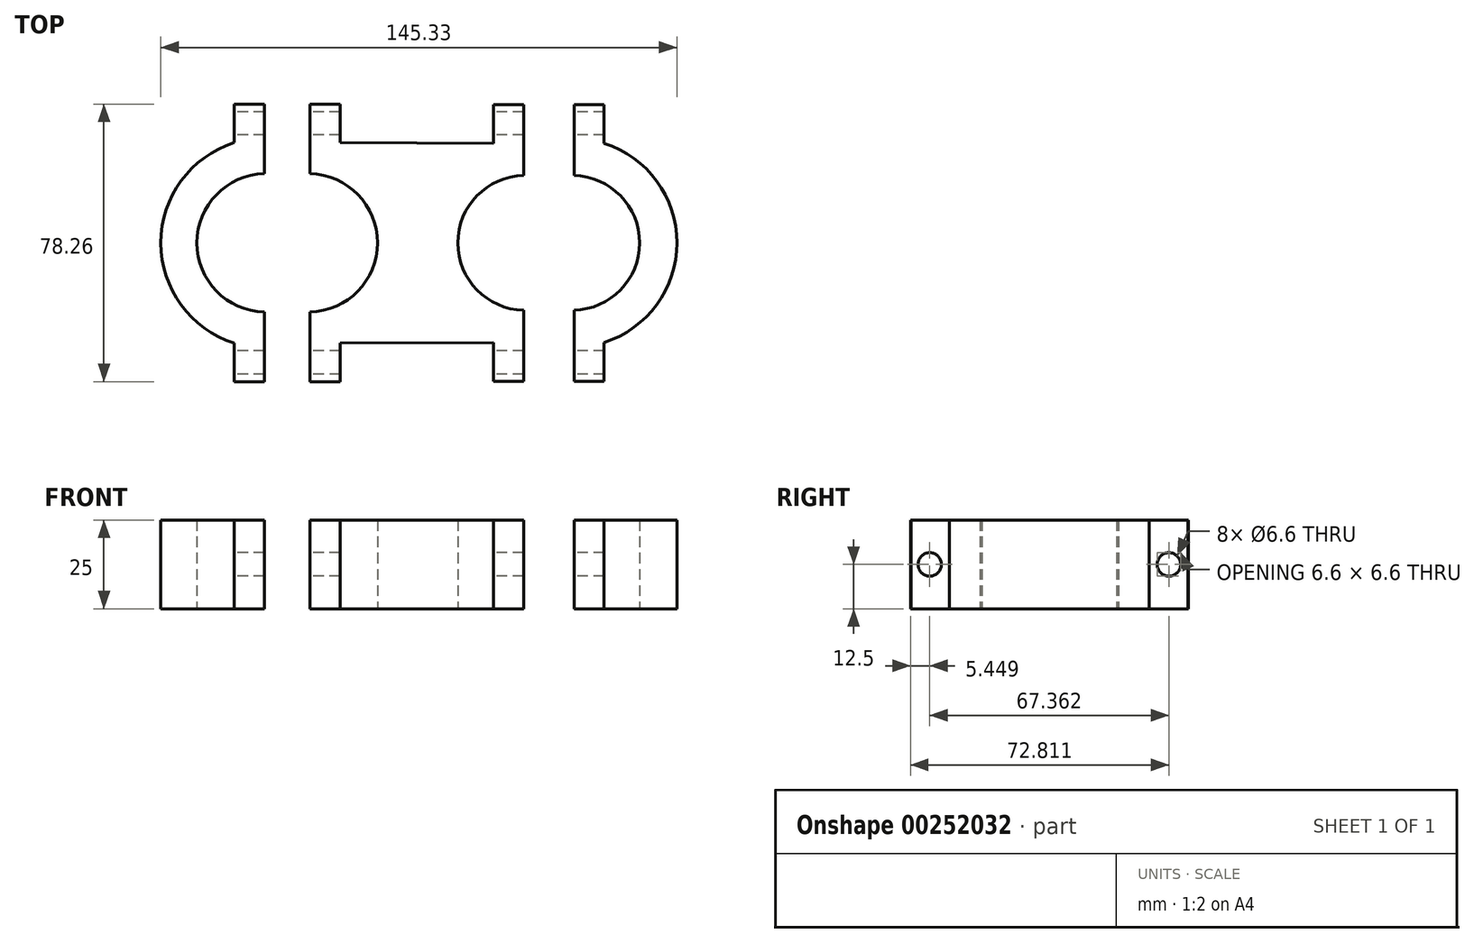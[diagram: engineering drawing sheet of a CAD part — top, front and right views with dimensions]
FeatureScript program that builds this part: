
annotation { "Feature Type Name" : "Feature", "Feature Type Description" : "" }
export const myFeature = defineFeature(function(context is Context, id is Id, definition is map)
    precondition{}
    {
        {
            var Q0;
            Q0=qCreatedBy(makeId("Top.planeOp"),FACE);
            var sketch = newSketch(context, id + "F0", { "sketchPlane" : qUnion([Q0])});
            skArc(sketch, "E0", {"start": v(-30.6, -29.63) * mm, "mid": v(-1, -0.23) * mm, "end": v(-30.13, 29.63) * mm});
            skLineSegment(sketch, "E1", {"start": v(-30.13, 39.13) * mm, "end": v(-21.63, 39.13) * mm});
            skLineSegment(sketch, "E2", {"start": v(-30.1, -39.13) * mm, "end": v(-21.6, -39.13) * mm});
            skLineSegment(sketch, "E3", {"start": v(-21.6, -39.13) * mm, "end": v(-21.6, -28.22) * mm});
            skLineSegment(sketch, "E4", {"start": v(-21.63, 39.13) * mm, "end": v(-21.63, 28.23) * mm});
            skLineSegment(sketch, "E5", {"start": v(30, 29.5) * mm, "end": v(30, 39) * mm});
            skLineSegment(sketch, "E6", {"start": v(30, 39) * mm, "end": v(21.5, 39) * mm});
            skLineSegment(sketch, "E7", {"start": v(30, -39) * mm, "end": v(21.5, -39) * mm});
            skArc(sketch, "E8", {"start": v(30, -29.5) * mm, "mid": v(1, 0) * mm, "end": v(30, 29.5) * mm});
            skLineSegment(sketch, "E9", {"start": v(21.5, 39) * mm, "end": v(21.5, 28.1) * mm});
            skLineSegment(sketch, "E10", {"start": v(21.5, -39) * mm, "end": v(21.5, -28.1) * mm});
            skLineSegment(sketch, "E11", {"start": v(-43, -39.13) * mm, "end": v(-51.5, -39.13) * mm});
            skLineSegment(sketch, "E12", {"start": v(-43, 39.13) * mm, "end": v(-51.5, 39.13) * mm});
            skArc(sketch, "E13", {"start": v(43.7, -29.5) * mm, "mid": v(73.2, -0.26) * mm, "end": v(44.22, 29.5) * mm});
            skArc(sketch, "E14", {"start": v(-42.5, -29.63) * mm, "mid": v(-72.13, -0.25) * mm, "end": v(-43, 29.63) * mm});
            skLineSegment(sketch, "E15", {"start": v(-51.5, 39.13) * mm, "end": v(-51.5, 28.23) * mm});
            skLineSegment(sketch, "E16", {"start": v(-51.5, -39.13) * mm, "end": v(-51.5, -28.23) * mm});
            skLineSegment(sketch, "E17", {"start": v(44.22, 29.5) * mm, "end": v(44.22, 39) * mm});
            skLineSegment(sketch, "E18", {"start": v(44.22, 39) * mm, "end": v(52.72, 39) * mm});
            skLineSegment(sketch, "E19", {"start": v(52.72, 39) * mm, "end": v(52.72, 28.09) * mm});
            skLineSegment(sketch, "E20", {"start": v(44.22, -39) * mm, "end": v(52.72, -39) * mm});
            skLineSegment(sketch, "E21", {"start": v(52.72, -39) * mm, "end": v(52.72, -28.09) * mm});
            skLineSegment(sketch, "E22", {"start": v(-43, 39.13) * mm, "end": v(-43, 29.63) * mm});
            skLineSegment(sketch, "E23", {"start": v(-30.13, 39.13) * mm, "end": v(-30.13, 29.63) * mm});
            skLineSegment(sketch, "E24", {"start": v(-43, -39.13) * mm, "end": v(-43, -29.63) * mm});
            skLineSegment(sketch, "E25", {"start": v(-43, -29.63) * mm, "end": v(-43, -19.5) * mm});
            skLineSegment(sketch, "E26", {"start": v(-43, 19.5) * mm, "end": v(-43, 29.63) * mm});
            skLineSegment(sketch, "E27", {"start": v(-30.13, 29.63) * mm, "end": v(-30.13, 19.5) * mm});
            skLineSegment(sketch, "E28", {"start": v(-30.13, -19.5) * mm, "end": v(-30.13, -29.63) * mm});
            skLineSegment(sketch, "E29", {"start": v(-30.13, -29.63) * mm, "end": v(-30.1, -39.13) * mm});
            skLineSegment(sketch, "E30", {"start": v(30, 29.5) * mm, "end": v(30, 19) * mm});
            skLineSegment(sketch, "E31", {"start": v(30, -19) * mm, "end": v(30, -29.5) * mm});
            skLineSegment(sketch, "E32", {"start": v(30, -29.5) * mm, "end": v(30, -39) * mm});
            skLineSegment(sketch, "E33", {"start": v(44.22, -39) * mm, "end": v(44.22, -29.5) * mm});
            skLineSegment(sketch, "E34", {"start": v(44.22, -29.5) * mm, "end": v(44.22, -19) * mm});
            skArc(sketch, "E35", {"start": v(-43, -19.5) * mm, "mid": v(-62, 0) * mm, "end": v(-43, 19.5) * mm});
            skArc(sketch, "E36", {"start": v(-30.13, -19.5) * mm, "mid": v(-11.12, 0) * mm, "end": v(-30.13, 19.5) * mm});
            skArc(sketch, "E37", {"start": v(30, -19) * mm, "mid": v(11.5, 0) * mm, "end": v(30, 19) * mm});
            skArc(sketch, "E38", {"start": v(44.22, -19) * mm, "mid": v(62.7, 0) * mm, "end": v(44.22, 19) * mm});
            skLineSegment(sketch, "E39", {"start": v(44.22, 19) * mm, "end": v(44.22, 29.5) * mm});
            skLineSegment(sketch, "E40", {"start": v(-1, 0) * mm, "end": v(0, 0) * mm});
            skLineSegment(sketch, "E41", {"start": v(0, 0) * mm, "end": v(1, 0) * mm});
            skLineSegment(sketch, "E42", {"start": v(1, 0) * mm, "end": v(0, 0) * mm});
            skLineSegment(sketch, "E43", {"start": v(-21.63, 28.23) * mm, "end": v(21.5, 28.1) * mm});
            skLineSegment(sketch, "E44", {"start": v(21.5, -28.1) * mm, "end": v(-21.6, -28.22) * mm});
            skSolve(sketch);
        }
        {
            var Q0;
            Q0 = qSketchRegion(id + "F0", true);
            extrude(context, id + "F1", {"entities" : qUnion([Q0]), "depth" : 25 * mm});
        }
        {
            var Q0;
            Q0=makeQuery(id+"F1.opExtrude","SWEPT_FACE",FACE,{"disambiguationData":[OSD([sQuery(id+"F0.wireOp",EDGE,"E15")])]});
            var sketch = newSketch(context, id + "F2", { "sketchPlane" : qUnion([Q0])});
            skPoint(sketch, "E45", {"position": v(-33.68, 12.5) * mm});
            skPoint(sketch, "E45.positionSnap0", {"position": v(-33.68, 25) * mm});
            skPoint(sketch, "E45.positionSnap1", {"position": v(-39.13, 12.5) * mm});
            skSolve(sketch);
        }
        {
            var Q0;
            Q0=makeQuery(id+"F1.opExtrude","SWEPT_FACE",FACE,{"disambiguationData":[OSD([sQuery(id+"F0.wireOp",EDGE,"E16")])]});
            var sketch = newSketch(context, id + "F3", { "sketchPlane" : qUnion([Q0])});
            skPoint(sketch, "E46", {"position": v(33.68, 12.5) * mm});
            skPoint(sketch, "E46.positionSnap0", {"position": v(28.23, 12.5) * mm});
            skPoint(sketch, "E46.positionSnap1", {"position": v(33.68, 25) * mm});
            skSolve(sketch);
        }
        {
            var Q0;
            Q0=sQuery(id+"F2.wireOp",VERTEX,"E45");
            var Q1;
            Q1=makeQuery(id+"F1.opExtrude","SWEPT_BODY",BODY,{"disambiguationData":[OSD([sQuery(id+"F0.wireOp",EDGE,"NLLKSBwt-9Cc3-8UtA-WMXZ-MWmgtgy61DwI"),sQuery(id+"F0.wireOp",EDGE,"mlnT00WE-T9qp-zRVp-k09w-XVGVqRZm4LCl"),sQuery(id+"F0.wireOp",EDGE,"x4fWWCr2-S3wZ-QtTH-78Jp-CiVb08rnXLRA"),sQuery(id+"F0.wireOp",EDGE,"Kp4KVj6V-pZQl-vQHE-af77-SHAt9ywuDPrm"),sQuery(id+"F0.wireOp",EDGE,"0mWQ3iTE-64RI-25Td-0Mzv-G9Ijoa3gPrGe"),sQuery(id+"F0.wireOp",EDGE,"E1"),sQuery(id+"F0.wireOp",EDGE,"E2"),sQuery(id+"F0.wireOp",EDGE,"E3"),sQuery(id+"F0.wireOp",EDGE,"E4"),sQuery(id+"F0.wireOp",EDGE,"turtuG6h-eshO-IJrb-mOBf-YkrXDYbMQhD5"),sQuery(id+"F0.wireOp",EDGE,"KMknyQUu-6qWn-A93p-KVvE-4iy4HAZ0i5xR"),sQuery(id+"F0.wireOp",EDGE,"E5"),sQuery(id+"F0.wireOp",EDGE,"E6"),sQuery(id+"F0.wireOp",EDGE,"BHHjrigB-iTKw-yMf5-cp13-6jmIiclecJZJ"),sQuery(id+"F0.wireOp",EDGE,"gnbI2XBb-As23-OZ3t-2CkV-z2erVP4Sxjtl"),sQuery(id+"F0.wireOp",EDGE,"E7"),sQuery(id+"F0.wireOp",EDGE,"E9"),sQuery(id+"F0.wireOp",EDGE,"E10"),sQuery(id+"F0.wireOp",EDGE,"tlpaueGA-kdq4-pMUM-cLeu-UnPulC1z7CFY"),sQuery(id+"F0.wireOp",EDGE,"VOcsD8bB-ICyP-ckm8-4KHL-qCeQyO8M8MDu")])]});
            var Q2;
            Q2=makeQuery(id+"F1.opExtrude","SWEPT_BODY",BODY,{"disambiguationData":[OSD([sQuery(id+"F0.wireOp",EDGE,"sJwOZ3o4-Ni56-aYj6-BFFI-69z3Aj2Iwr6m"),sQuery(id+"F0.wireOp",EDGE,"QYwanN3T-Wy01-M6QR-H8Kc-KS6hqBJ2BEqt"),sQuery(id+"F0.wireOp",EDGE,"E11"),sQuery(id+"F0.wireOp",EDGE,"E12"),sQuery(id+"F0.wireOp",EDGE,"Ioq0ThUd-jbmS-MYdZ-EBiQ-QcwC0IldSgJW"),sQuery(id+"F0.wireOp",EDGE,"E14"),sQuery(id+"F0.wireOp",EDGE,"E15"),sQuery(id+"F0.wireOp",EDGE,"E16"),sQuery(id+"F0.wireOp",EDGE,"0r23HsPS-85FX-V7Rp-pwcG-1QWv6BM0zKr3"),sQuery(id+"F0.wireOp",EDGE,"D1FhsTZA-RR5G-TxYw-mrW1-opwHyA07geDs")])]});
            var Q3;
            Q3=makeQuery(id+"F1.opExtrude","SWEPT_BODY",BODY,{"disambiguationData":[OSD([sQuery(id+"F0.wireOp",EDGE,"SS6wCFSk-3bHG-TTAv-AyRD-yDFx4wt1FxYl"),sQuery(id+"F0.wireOp",EDGE,"6hV5W4a7-xWOT-snzw-M7rb-nCtUfnUzwPGj"),sQuery(id+"F0.wireOp",EDGE,"C2QgIaAH-yhjf-IMJu-Hzuo-EfdFIp6Fg8OY"),sQuery(id+"F0.wireOp",EDGE,"E13"),sQuery(id+"F0.wireOp",EDGE,"JkAYAIaF-GpBp-aERu-hlCk-zMQrTZ84ZjXN"),sQuery(id+"F0.wireOp",EDGE,"E17"),sQuery(id+"F0.wireOp",EDGE,"E18"),sQuery(id+"F0.wireOp",EDGE,"E19"),sQuery(id+"F0.wireOp",EDGE,"E20"),sQuery(id+"F0.wireOp",EDGE,"E21")])]});
            hole(context, id + "F4", {"style" : HoleStyle.SIMPLE, "endStyle" : HoleEndStyle.THROUGH, "standardTappedOrClearance" : lookupTablePath({ "standard" : "ISO", "fit" : "Normal", "size" : "M6", "type" : "Clearance" }), "standardBlindInLast" : lookupTablePath({ "fit" : "Standard", "standard" : "ISO", "size" : "M6", "type" : "Clearance" }), "holeDiameter" : 6.6 * mm, "tappedDepth" : 12 * mm, "tapClearance" : 3, "locations" : qUnion([Q0]), "scope" : qUnion([Q1, Q2, Q3])});
        }
        {
            var Q0;
            Q0=sQuery(id+"F3.wireOp",VERTEX,"E46");
            var Q1;
            Q1=makeQuery(id+"F1.opExtrude","SWEPT_BODY",BODY,{"disambiguationData":[OSD([sQuery(id+"F0.wireOp",EDGE,"NLLKSBwt-9Cc3-8UtA-WMXZ-MWmgtgy61DwI"),sQuery(id+"F0.wireOp",EDGE,"mlnT00WE-T9qp-zRVp-k09w-XVGVqRZm4LCl"),sQuery(id+"F0.wireOp",EDGE,"x4fWWCr2-S3wZ-QtTH-78Jp-CiVb08rnXLRA"),sQuery(id+"F0.wireOp",EDGE,"Kp4KVj6V-pZQl-vQHE-af77-SHAt9ywuDPrm"),sQuery(id+"F0.wireOp",EDGE,"0mWQ3iTE-64RI-25Td-0Mzv-G9Ijoa3gPrGe"),sQuery(id+"F0.wireOp",EDGE,"E1"),sQuery(id+"F0.wireOp",EDGE,"E2"),sQuery(id+"F0.wireOp",EDGE,"E3"),sQuery(id+"F0.wireOp",EDGE,"E4"),sQuery(id+"F0.wireOp",EDGE,"turtuG6h-eshO-IJrb-mOBf-YkrXDYbMQhD5"),sQuery(id+"F0.wireOp",EDGE,"KMknyQUu-6qWn-A93p-KVvE-4iy4HAZ0i5xR"),sQuery(id+"F0.wireOp",EDGE,"E5"),sQuery(id+"F0.wireOp",EDGE,"E6"),sQuery(id+"F0.wireOp",EDGE,"BHHjrigB-iTKw-yMf5-cp13-6jmIiclecJZJ"),sQuery(id+"F0.wireOp",EDGE,"gnbI2XBb-As23-OZ3t-2CkV-z2erVP4Sxjtl"),sQuery(id+"F0.wireOp",EDGE,"E7"),sQuery(id+"F0.wireOp",EDGE,"E9"),sQuery(id+"F0.wireOp",EDGE,"E10"),sQuery(id+"F0.wireOp",EDGE,"tlpaueGA-kdq4-pMUM-cLeu-UnPulC1z7CFY"),sQuery(id+"F0.wireOp",EDGE,"VOcsD8bB-ICyP-ckm8-4KHL-qCeQyO8M8MDu")])]});
            var Q2;
            Q2=makeQuery(id+"F1.opExtrude","SWEPT_BODY",BODY,{"disambiguationData":[OSD([sQuery(id+"F0.wireOp",EDGE,"sJwOZ3o4-Ni56-aYj6-BFFI-69z3Aj2Iwr6m"),sQuery(id+"F0.wireOp",EDGE,"QYwanN3T-Wy01-M6QR-H8Kc-KS6hqBJ2BEqt"),sQuery(id+"F0.wireOp",EDGE,"E11"),sQuery(id+"F0.wireOp",EDGE,"E12"),sQuery(id+"F0.wireOp",EDGE,"Ioq0ThUd-jbmS-MYdZ-EBiQ-QcwC0IldSgJW"),sQuery(id+"F0.wireOp",EDGE,"E14"),sQuery(id+"F0.wireOp",EDGE,"E15"),sQuery(id+"F0.wireOp",EDGE,"E16"),sQuery(id+"F0.wireOp",EDGE,"0r23HsPS-85FX-V7Rp-pwcG-1QWv6BM0zKr3"),sQuery(id+"F0.wireOp",EDGE,"D1FhsTZA-RR5G-TxYw-mrW1-opwHyA07geDs")])]});
            var Q3;
            Q3=makeQuery(id+"F1.opExtrude","SWEPT_BODY",BODY,{"disambiguationData":[OSD([sQuery(id+"F0.wireOp",EDGE,"SS6wCFSk-3bHG-TTAv-AyRD-yDFx4wt1FxYl"),sQuery(id+"F0.wireOp",EDGE,"6hV5W4a7-xWOT-snzw-M7rb-nCtUfnUzwPGj"),sQuery(id+"F0.wireOp",EDGE,"C2QgIaAH-yhjf-IMJu-Hzuo-EfdFIp6Fg8OY"),sQuery(id+"F0.wireOp",EDGE,"E13"),sQuery(id+"F0.wireOp",EDGE,"JkAYAIaF-GpBp-aERu-hlCk-zMQrTZ84ZjXN"),sQuery(id+"F0.wireOp",EDGE,"E17"),sQuery(id+"F0.wireOp",EDGE,"E18"),sQuery(id+"F0.wireOp",EDGE,"E19"),sQuery(id+"F0.wireOp",EDGE,"E20"),sQuery(id+"F0.wireOp",EDGE,"E21")])]});
            hole(context, id + "F5", {"style" : HoleStyle.SIMPLE, "endStyle" : HoleEndStyle.THROUGH, "standardTappedOrClearance" : lookupTablePath({ "standard" : "ISO", "fit" : "Normal", "size" : "M6", "type" : "Clearance" }), "standardBlindInLast" : lookupTablePath({ "fit" : "Standard", "standard" : "ISO", "size" : "M6", "type" : "Clearance" }), "holeDiameter" : 6.6 * mm, "tappedDepth" : 12 * mm, "tapClearance" : 3, "locations" : qUnion([Q0]), "scope" : qUnion([Q1, Q2, Q3])});
        }
    });
